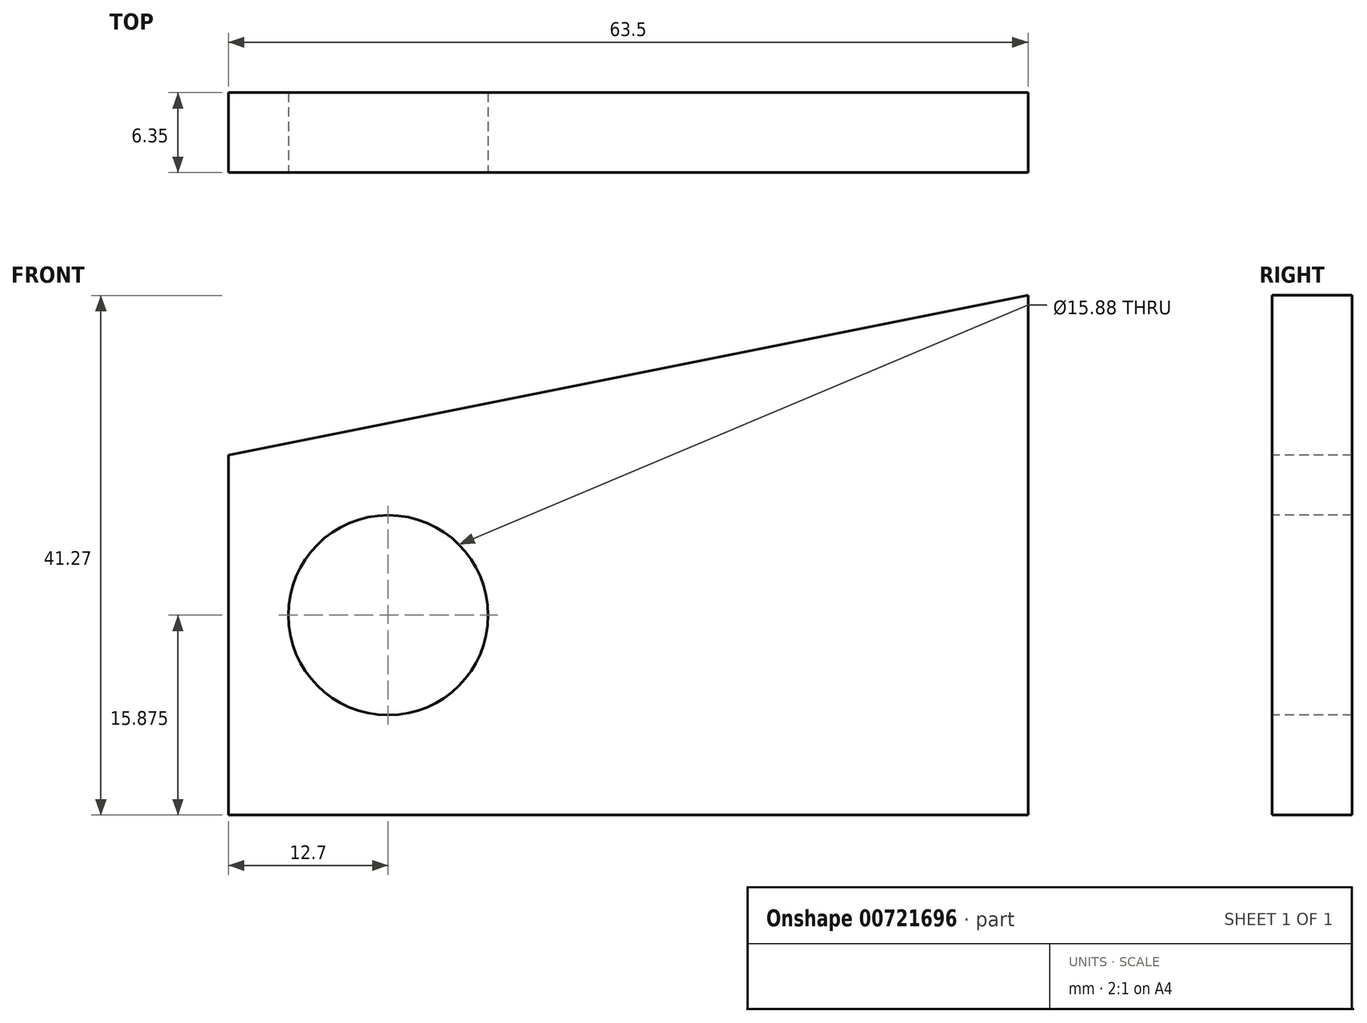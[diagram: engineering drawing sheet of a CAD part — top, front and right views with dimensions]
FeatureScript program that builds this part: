
annotation { "Feature Type Name" : "Feature", "Feature Type Description" : "" }
export const myFeature = defineFeature(function(context is Context, id is Id, definition is map)
    precondition{}
    {
        {
            var Q0;
            Q0=qCreatedBy(makeId("Front.planeOp"),FACE);
            var sketch = newSketch(context, id + "F0", { "sketchPlane" : qUnion([Q0])});
            skLineSegment(sketch, "E0", {"start": v(63.5, 41.27) * mm, "end": v(0, 28.58) * mm});
            skLineSegment(sketch, "E1", {"start": v(-23.36, 15.88) * mm, "end": v(107.5, 15.88) * mm, "construction": true});
            skLineSegment(sketch, "E2", {"start": v(12.7, 88.01) * mm, "end": v(12.7, -6.79) * mm, "construction": true});
            skCircle(sketch, "E3", {"center": v(12.7, 15.88) * mm, "radius": 7.94 * mm});
            skLineSegment(sketch, "E4", {"start": v(0, 0) * mm, "end": v(63.5, 0) * mm});
            skLineSegment(sketch, "E5", {"start": v(0, 28.58) * mm, "end": v(0, 0) * mm});
            skLineSegment(sketch, "E6", {"start": v(63.5, 41.27) * mm, "end": v(63.5, 0) * mm});
            skSolve(sketch);
        }
        {
            var Q0;
            Q0 = qSketchRegion(id + "F0", true);
            extrude(context, id + "F1", {"entities" : qUnion([Q0]), "oppositeDirection" : true, "depth" : 6.35 * mm, "offsetDistance" : 25.4 * mm});
        }
    });
